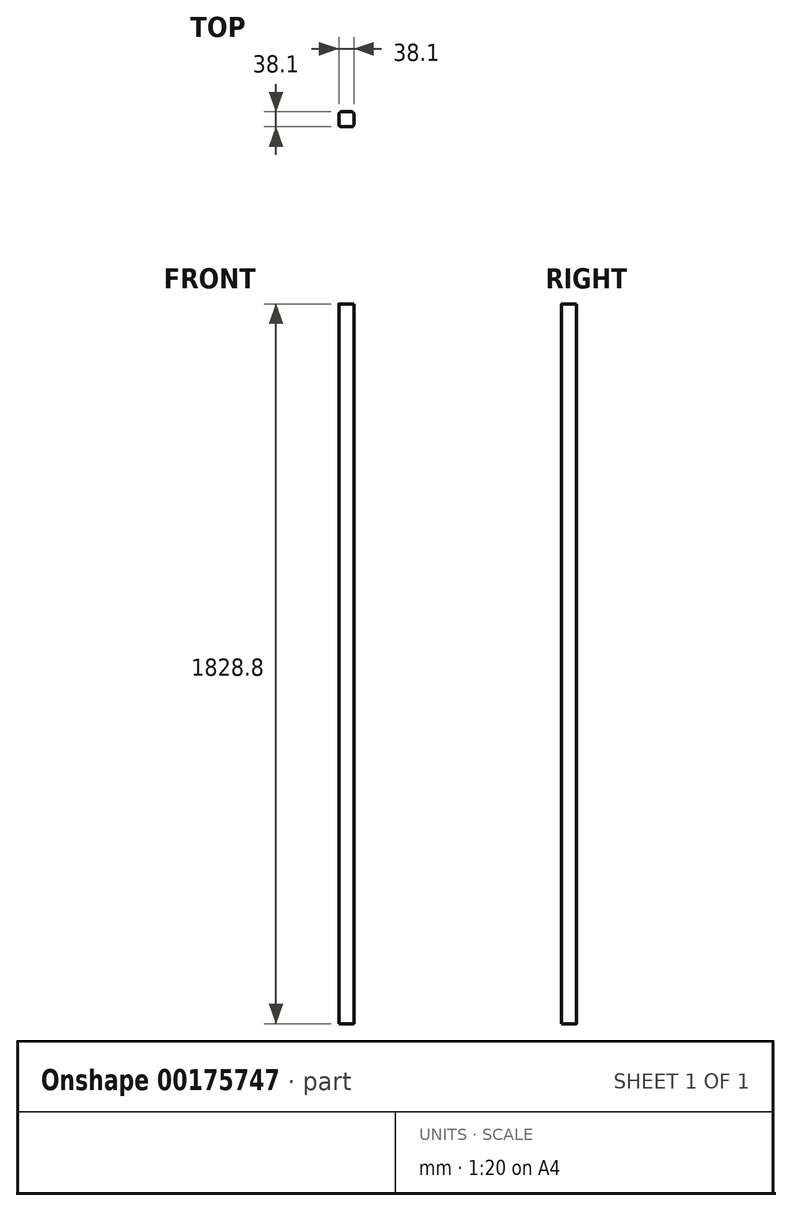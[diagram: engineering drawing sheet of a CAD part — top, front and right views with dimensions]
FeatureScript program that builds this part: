
annotation { "Feature Type Name" : "Feature", "Feature Type Description" : "" }
export const myFeature = defineFeature(function(context is Context, id is Id, definition is map)
    precondition{}
    {
        {
            var Q0;
            Q0=qCreatedBy(makeId("Top.planeOp"),FACE);
            var sketch = newSketch(context, id + "F0", { "sketchPlane" : qUnion([Q0])});
            skLineSegment(sketch, "E0.bottom", {"start": v(12.7, 19.05) * mm, "end": v(-12.7, 19.05) * mm});
            skLineSegment(sketch, "E0.top", {"start": v(12.7, -19.05) * mm, "end": v(-12.7, -19.05) * mm});
            skLineSegment(sketch, "E0.left", {"start": v(19.05, 12.7) * mm, "end": v(19.05, -12.7) * mm});
            skLineSegment(sketch, "E0.right", {"start": v(-19.05, 12.7) * mm, "end": v(-19.05, -12.7) * mm});
            skPoint(sketch, "E0.middle", {"position": v(0, 0) * mm});
            skPoint(sketch, "E1.visualSharp", {"position": v(-19.05, 19.05) * mm});
            skArc(sketch, "E1.filletArc", {"start": v(-12.7, 19.05) * mm, "mid": v(-17.2, 17.2) * mm, "end": v(-19.05, 12.7) * mm});
            skPoint(sketch, "E2.visualSharp", {"position": v(19.05, 19.05) * mm});
            skArc(sketch, "E2.filletArc", {"start": v(19.05, 12.7) * mm, "mid": v(17.2, 17.2) * mm, "end": v(12.7, 19.05) * mm});
            skPoint(sketch, "E3.visualSharp", {"position": v(19.05, -19.05) * mm});
            skArc(sketch, "E3.filletArc", {"start": v(12.7, -19.05) * mm, "mid": v(17.2, -17.2) * mm, "end": v(19.05, -12.7) * mm});
            skPoint(sketch, "E4.visualSharp", {"position": v(-19.05, -19.05) * mm});
            skArc(sketch, "E4.filletArc", {"start": v(-19.05, -12.7) * mm, "mid": v(-17.2, -17.2) * mm, "end": v(-12.7, -19.05) * mm});
            skSolve(sketch);
        }
        {
            var Q0;
            Q0 = qSketchRegion(id + "F0", true);
            extrude(context, id + "F1", {"entities" : qUnion([Q0]), "depth" : 1828.8 * mm});
        }
    });
